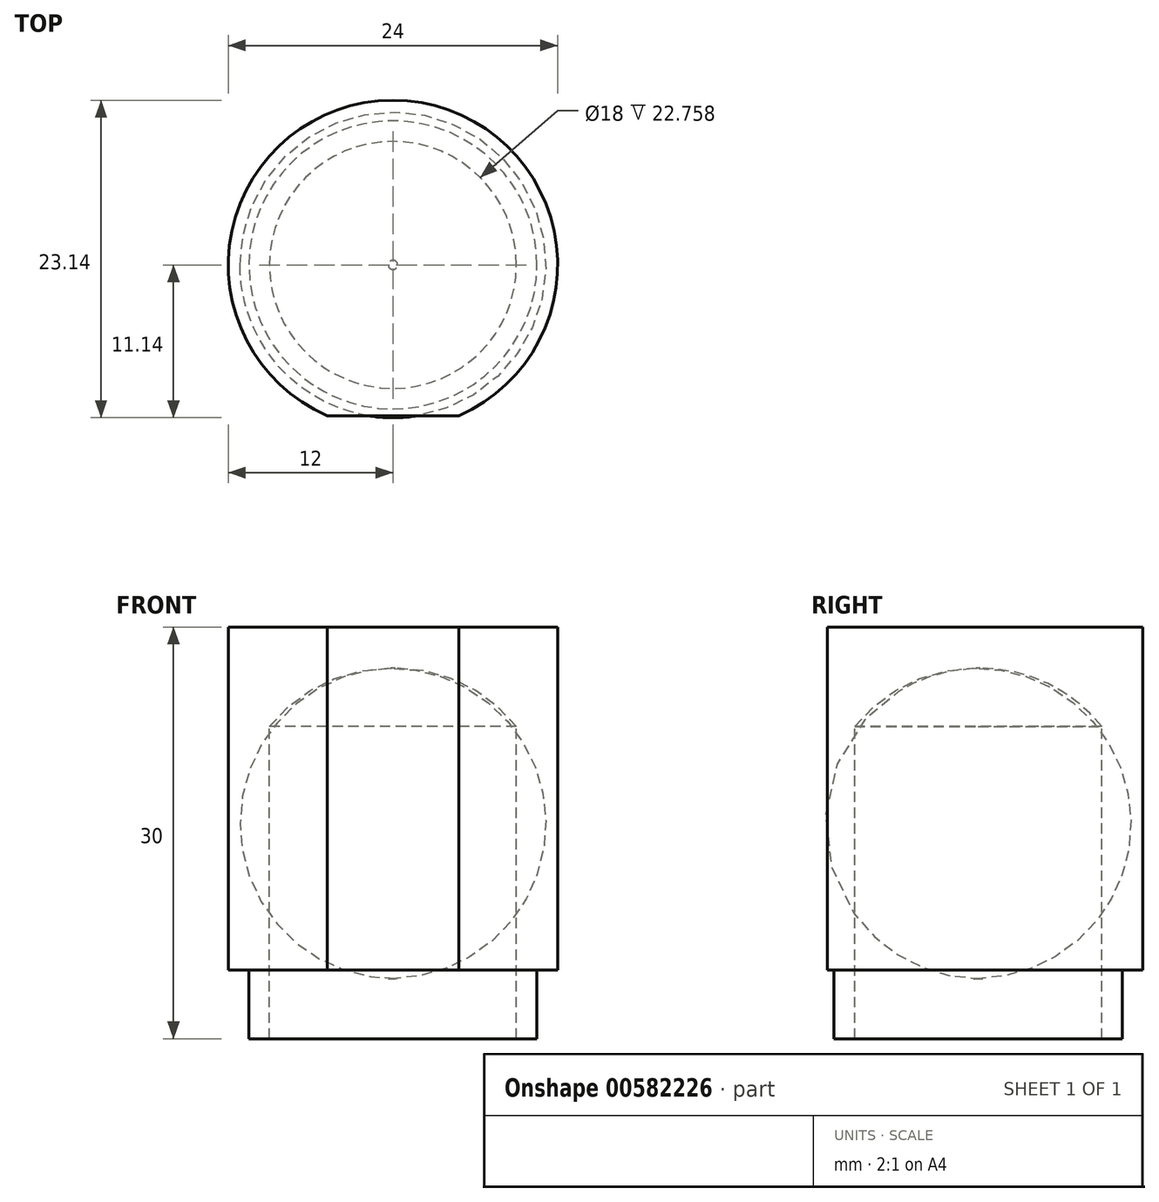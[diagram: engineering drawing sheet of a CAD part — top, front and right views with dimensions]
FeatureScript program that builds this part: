
annotation { "Feature Type Name" : "Feature", "Feature Type Description" : "" }
export const myFeature = defineFeature(function(context is Context, id is Id, definition is map)
    precondition{}
    {
        {
            var Q0;
            Q0=qCreatedBy(makeId("Front.planeOp"),FACE);
            var sketch = newSketch(context, id + "F0", { "sketchPlane" : qUnion([Q0]), "disableImprinting" : false});
            skLineSegment(sketch, "E0.MirrorCS", {"start": v(-10.5, -25) * mm, "end": v(-12, -25) * mm});
            skLineSegment(sketch, "E1", {"start": v(-12, -3) * mm, "end": v(-12, 0) * mm});
            skLineSegment(sketch, "E2", {"start": v(-12, -3) * mm, "end": v(-12, -25) * mm});
            skLineSegment(sketch, "E3", {"start": v(-10.5, -25) * mm, "end": v(-10.5, -30) * mm});
            skLineSegment(sketch, "E4", {"start": v(-10.5, -30) * mm, "end": v(-9, -30) * mm});
            skLineSegment(sketch, "E5", {"start": v(-12, 0) * mm, "end": v(0, 0) * mm});
            skLineSegment(sketch, "E6.MirrorCS", {"start": v(10.5, -25) * mm, "end": v(10.5, -30) * mm});
            skLineSegment(sketch, "E7.MirrorCS", {"start": v(12, 0) * mm, "end": v(-3, 0) * mm});
            skLineSegment(sketch, "E8.MirrorCS", {"start": v(12, -3) * mm, "end": v(12, -25) * mm});
            skLineSegment(sketch, "E9.MirrorCS", {"start": v(10.5, -25) * mm, "end": v(12, -25) * mm});
            skLineSegment(sketch, "E10.MirrorCS", {"start": v(12, -3) * mm, "end": v(12, 0) * mm});
            skLineSegment(sketch, "E11.MirrorCS", {"start": v(10.5, -30) * mm, "end": v(9, -30) * mm});
            skArc(sketch, "E12", {"start": v(9, -7.69) * mm, "mid": v(0.11, -3) * mm, "end": v(-9, -7.24) * mm});
            skLineSegment(sketch, "E13", {"start": v(-9, -30) * mm, "end": v(-9, -7.24) * mm});
            skLineSegment(sketch, "E14", {"start": v(9, -30) * mm, "end": v(9, -7.69) * mm});
            skLineSegment(sketch, "E15", {"start": v(0, 0) * mm, "end": v(0, -3) * mm});
            skSolve(sketch);
        }
        {
            var Q0;
            {var subQ0=sQuery(id+"F0.wireOp",EDGE,"I7DhDJuf-7NLr-Svl4-PwQn-US4yEfDLbxPE.left");Q0=makeQuery(id+"F0.imprint","IMPRINT",FACE,{"disambiguationData":[TD([[makeQuery(id+"F0.imprint","IMPRINT",EDGE,{"derivedFrom":subQ0}),-1.0]])]});}
            var Q1;
            Q1=makeQuery(id+"F0.imprint","IMPRINT",FACE,{"disambiguationData":[TD([[makeQuery(id+"F0.imprint","IMPRINT",EDGE,{"derivedFrom":sQuery(id+"F0.wireOp",EDGE,"32eac864-653d-4b33-877a-62f6442f8a590.MirrorCS")}),1.0]])]});
            var Q2;
            Q2=makeQuery(id+"F0.imprint","IMPRINT",FACE,{"disambiguationData":[TD([[makeQuery(id+"F0.imprint","IMPRINT",EDGE,{"derivedFrom":sQuery(id+"F0.wireOp",EDGE,"E0.MirrorCS")}),-1.0]])]});
            var Q3;
            Q3=sQuery(id+"F0.wireOp",EDGE,"E15");
            revolve(context, id + "F1", {"entities" : qUnion([Q0, Q1, Q2]), "axis" : qUnion([Q3]), "revolveType" : RevolveType.FULL});
        }
        {
            var Q0;
            Q0=makeQuery(id+"F1.opRevolve","SWEPT_FACE",FACE,{"disambiguationData":[OSD([sQuery(id+"F0.wireOp",EDGE,"E0.MirrorCS")])]});
            var sketch = newSketch(context, id + "F2", { "sketchPlane" : qUnion([Q0])});
            skLineSegment(sketch, "E16.bottom", {"start": v(0, 11) * mm, "end": v(5, 11) * mm});
            skLineSegment(sketch, "E16.top", {"start": v(0, 12.77) * mm, "end": v(5, 12.77) * mm});
            skLineSegment(sketch, "E16.right", {"start": v(5, 11) * mm, "end": v(5, 12.77) * mm});
            skLineSegment(sketch, "E17.MirrorCS", {"start": v(-5, 11) * mm, "end": v(-5, 12.77) * mm});
            skLineSegment(sketch, "E18.MirrorCS", {"start": v(0, 12.77) * mm, "end": v(-5, 12.77) * mm});
            skLineSegment(sketch, "E19.MirrorCS", {"start": v(0, 11) * mm, "end": v(-5, 11) * mm});
            skSolve(sketch);
        }
        {
            var Q0;
            Q0 = qSketchRegion(id + "F2", true);
            extrude(context, id + "F3", {"entities" : qUnion([Q0]), "operationType" : NewBodyOperationType.REMOVE, "oppositeDirection" : true, "depth" : 25 * mm, "offsetDistance" : 25 * mm});
        }
    });
